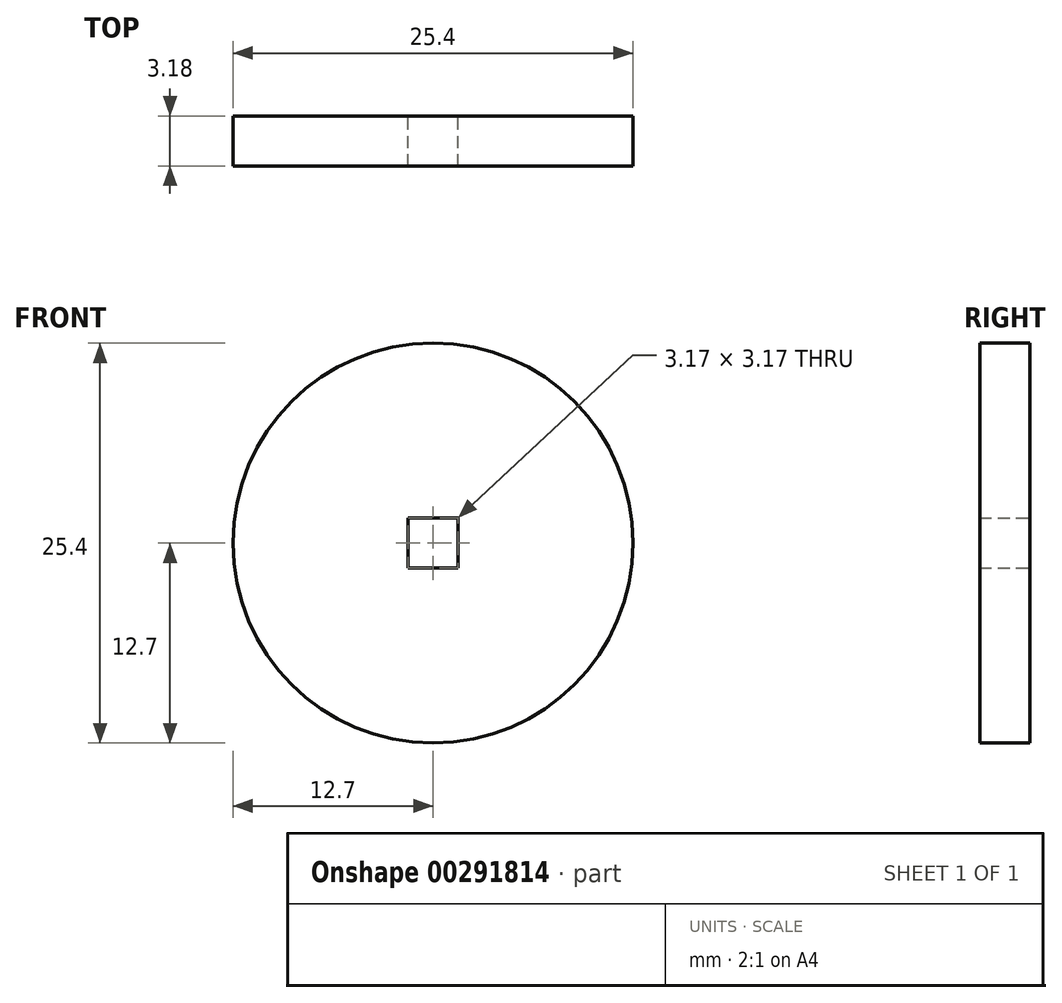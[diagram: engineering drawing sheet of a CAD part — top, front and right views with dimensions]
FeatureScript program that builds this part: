
annotation { "Feature Type Name" : "Feature", "Feature Type Description" : "" }
export const myFeature = defineFeature(function(context is Context, id is Id, definition is map)
    precondition{}
    {
        {
            var Q0;
            Q0=qCreatedBy(makeId("Front.planeOp"),FACE);
            var sketch = newSketch(context, id + "F0", { "sketchPlane" : qUnion([Q0])});
            skCircle(sketch, "E0", {"center": v(0, 0) * mm, "radius": 12.7 * mm});
            skSolve(sketch);
        }
        {
            var Q0;
            Q0 = qSketchRegion(id + "F0", true);
            extrude(context, id + "F1", {"entities" : qUnion([Q0]), "endBound" : BoundingType.SYMMETRIC, "depth" : 3.17 * mm});
        }
        {
            var Q0;
            Q0=makeQuery(id+"F1.opExtrude","CAP_FACE",FACE,{"disambiguationData":[OSD([sQuery(id+"F0.wireOp",EDGE,"E0")])],"isStart":true});
            var sketch = newSketch(context, id + "F2", { "sketchPlane" : qUnion([Q0])});
            skLineSegment(sketch, "E1.bottom", {"start": v(1.59, 1.59) * mm, "end": v(-1.59, 1.59) * mm});
            skLineSegment(sketch, "E1.top", {"start": v(1.59, -1.59) * mm, "end": v(-1.59, -1.59) * mm});
            skLineSegment(sketch, "E1.left", {"start": v(1.59, 1.59) * mm, "end": v(1.59, -1.59) * mm});
            skLineSegment(sketch, "E1.right", {"start": v(-1.59, 1.59) * mm, "end": v(-1.59, -1.59) * mm});
            skPoint(sketch, "E1.middle", {"position": v(0, 0) * mm});
            skSolve(sketch);
        }
        {
            var Q0;
            Q0 = qSketchRegion(id + "F2", true);
            extrude(context, id + "F3", {"entities" : qUnion([Q0]), "operationType" : NewBodyOperationType.REMOVE, "endBound" : BoundingType.THROUGH_ALL, "oppositeDirection" : true, "depth" : 25.4 * mm});
        }
    });
